# Revit family: LEO_D_XL_RFA_2019
name_source: partatom
category: Mechanical Equipment
units: mm (PartAtom-declared; Revit-internal decimal feet)

## family parameters
Cut with Voids When Loaded = No
Host = Face
Part Type = Normal
Room Calculation Point = No
Round Connector Dimension = Use Diameter
Shared = No

## types (9) — shared parameters
Description = Destratifikátor
Distance from the ceiling = 1000 mm  [stored 3.28084 ft]
Fan = axial, single-phase, AC with 3-speed motor
IP = 54
Load classification = Silnik
Manufacturer = Hydronic Systems Prague s.r.o.
Mass of unit = 19.50 kg
Material = EPP-grey
Power factor = 1
Supply voltage = 230 V
Type Comments = vnitřní instalace, podstropní, vertikální; max. teplota okolí +50°C; IP54; Qmax=7200 m3/h při 3. rychlosti
URL = www.hydronic.cz
zero-valued in all types: Default Elevation

## per-type parameters (varying)
| type | Airflow | Apparent power | Assembly Code | Max. current consumption | Model | Standard equipment |
| LEO DT XL, 1 rychlost | 3900.0 m³/h | 322 VA | 52077; LEO DT XL (vč. integrovaného pokojového termostatu)  - 1 rychlost | 1 A | LEO DT XL | pokojový termostat umístěný na opláštění jednotky |
| LEO DT XL, 2 rychlost | 6100.0 m³/h | 345 VA | 52077; LEO DT XL (vč. integrovaného pokojového termostatu)  - 2 rychlost | 2 A | LEO DT XL | pokojový termostat umístěný na opláštění jednotky |
| LEO DT XL, 3 rychlost | 7200.0 m³/h | 460 VA | 52077; LEO DT XL (vč. integrovaného pokojového termostatu)  - 3 rychlost | 2 A | LEO DT XL | pokojový termostat umístěný na opláštění jednotky |
| LEO D XL BMS, 1 rychlost | 3900.0 m³/h | 322 VA | 52082; LEO D XL BMS (vč. DRV-D + 1xPT1000)  - 1 rychlost | 1 A | LEO D XL BMS | DRV D + PT-1000 |
| LEO D XL BMS, 2 rychlost | 6100.0 m³/h | 345 VA | 52082; LEO D XL BMS (vč. DRV-D + 1xPT1000)  - 2 rychlost | 2 A | LEO D XL BMS | DRV D + PT-1000 |
| LEO D XL BMS, 3 rychlost | 7200.0 m³/h | 460 VA | 52082; LEO D XL BMS (vč. DRV-D + 1xPT1000)  - 3 rychlost | 2 A | LEO D XL BMS | DRV D + PT-1000 |
| LEO D XL, 1 rychlost | 3900.0 m³/h | 322 VA | 52072; LEO D XL  - 1 rychlost | 1 A | LEO D XL |  |
| LEO D XL, 2 rychlost | 6100.0 m³/h | 345 VA | 52072; LEO D XL  - 2 rychlost | 2 A | LEO D XL |  |
| LEO D XL, 3 rychlost | 7200.0 m³/h | 460 VA | 52072; LEO D XL  - 3 rychlost | 2 A | LEO D XL |  |

note: [stored X ft] marks values corroborated as IEEE doubles in the binary element streams (Revit-internal decimal feet)
